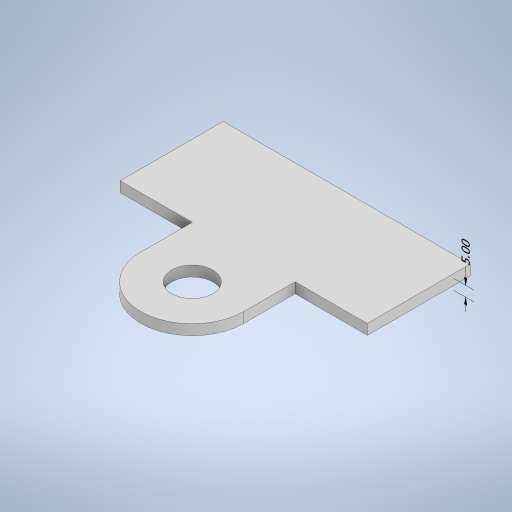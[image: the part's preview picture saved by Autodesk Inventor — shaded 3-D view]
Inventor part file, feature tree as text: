
AUTODESK INVENTOR PART (.ipt)
format: ipt  version: 2024.1 (Build 281209000, 209)  size: 269,824 bytes
history: native  units: mm
features: other x2, extrude x2, sketch x2
ambient origin geometry x8: Origin, YZ Plane, XZ Plane, XY Plane, X Axis, Y Axis, Z Axis, Center Point
bodies: Body1 (feature_tree)
feature tree (6):
  other  "ソリッド1"
  extrude  "押し出し1"  Depth=114.0mm
  extrude  "押し出し4"  Depth=150.0mm
  sketch  "スケッチ1"
  sketch  "スケッチ4"
  other  "長さ寸法 2"
